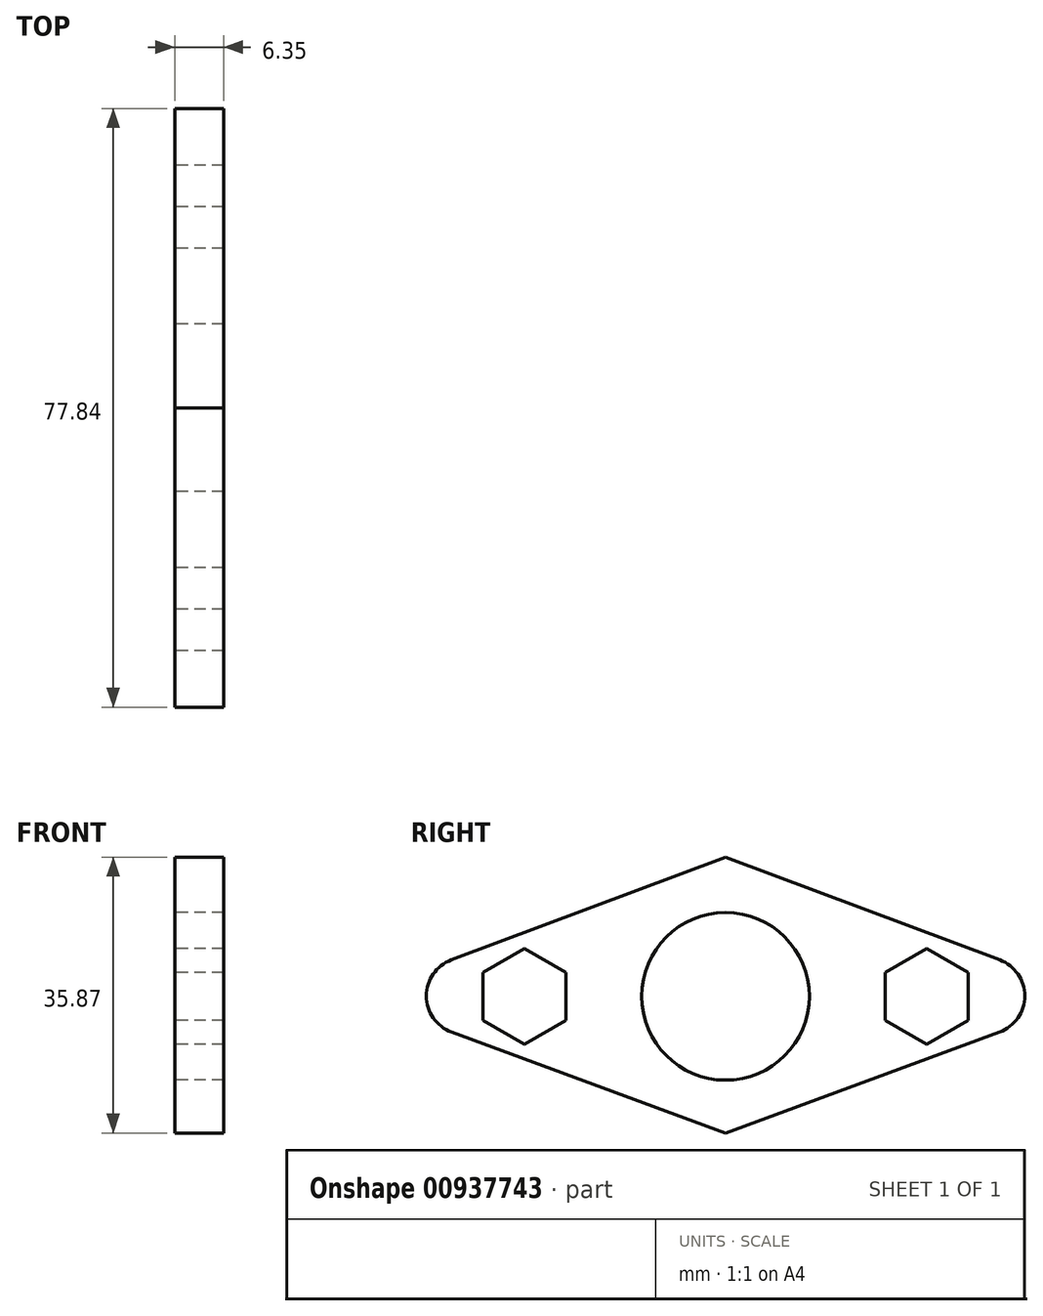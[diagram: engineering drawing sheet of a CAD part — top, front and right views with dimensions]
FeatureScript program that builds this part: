
annotation { "Feature Type Name" : "Feature", "Feature Type Description" : "" }
export const myFeature = defineFeature(function(context is Context, id is Id, definition is map)
    precondition{}
    {
        {
            var Q0;
            Q0=qCreatedBy(makeId("Right.planeOp"),FACE);
            var sketch = newSketch(context, id + "F0", { "sketchPlane" : qUnion([Q0])});
            skPoint(sketch, "E0.start.orphan", {"position": v(-59.2, 0) * mm});
            skPoint(sketch, "E1.end.orphan", {"position": v(60.96, 0) * mm});
            skPoint(sketch, "E2.end.orphan", {"position": v(0, 18.1) * mm});
            skPoint(sketch, "E3.end.orphan", {"position": v(0, -17.77) * mm});
            skCircle(sketch, "E4", {"center": v(0, 0) * mm, "radius": 10.9 * mm});
            skCircle(sketch, "E5.cCircle", {"center": v(26.15, 0) * mm, "radius": 5.4 * mm, "construction": true});
            skLineSegment(sketch, "E5.0", {"start": v(20.75, -3.12) * mm, "end": v(20.75, 3.12) * mm});
            skLineSegment(sketch, "E5.1", {"start": v(20.75, 3.12) * mm, "end": v(26.15, 6.24) * mm});
            skLineSegment(sketch, "E5.2", {"start": v(26.15, 6.24) * mm, "end": v(31.55, 3.12) * mm});
            skLineSegment(sketch, "E5.3", {"start": v(31.55, 3.12) * mm, "end": v(31.55, -3.12) * mm});
            skLineSegment(sketch, "E5.4", {"start": v(31.55, -3.12) * mm, "end": v(26.15, -6.24) * mm});
            skLineSegment(sketch, "E5.5", {"start": v(26.15, -6.24) * mm, "end": v(20.75, -3.12) * mm});
            skCircle(sketch, "E6.MirrorC", {"center": v(-26.15, 0) * mm, "radius": 5.4 * mm, "construction": true});
            skLineSegment(sketch, "E7.MirrorCS", {"start": v(-26.15, -6.24) * mm, "end": v(-20.75, -3.12) * mm});
            skLineSegment(sketch, "E8.MirrorCS", {"start": v(-20.75, -3.12) * mm, "end": v(-20.75, 3.12) * mm});
            skLineSegment(sketch, "E9.MirrorCS", {"start": v(-20.75, 3.12) * mm, "end": v(-26.15, 6.24) * mm});
            skLineSegment(sketch, "E10.MirrorCS", {"start": v(-26.15, 6.24) * mm, "end": v(-31.55, 3.12) * mm});
            skLineSegment(sketch, "E11.MirrorCS", {"start": v(-31.55, 3.12) * mm, "end": v(-31.55, -3.12) * mm});
            skLineSegment(sketch, "E12.MirrorCS", {"start": v(-31.55, -3.12) * mm, "end": v(-26.15, -6.24) * mm});
            skLineSegment(sketch, "E13", {"start": v(0, 18.1) * mm, "end": v(-48.27, 0) * mm});
            skLineSegment(sketch, "E14", {"start": v(-48.27, 0) * mm, "end": v(0, -17.77) * mm});
            skLineSegment(sketch, "E15.MirrorCS", {"start": v(0, 18.1) * mm, "end": v(48.27, 0) * mm});
            skLineSegment(sketch, "E16.MirrorCS", {"start": v(48.27, 0) * mm, "end": v(0, -17.77) * mm});
            skSolve(sketch);
        }
        {
            var Q0;
            Q0=makeQuery(id+"F0.imprint","IMPRINT",FACE,{"disambiguationData":[TD([[makeQuery(id+"F0.imprint","IMPRINT",EDGE,{"derivedFrom":sQuery(id+"F0.wireOp",EDGE,"E4")}),-1.0]])]});
            extrude(context, id + "F1", {"entities" : qUnion([Q0]), "depth" : 6.35 * mm, "offsetDistance" : 25 * mm});
        }
        {
            var Q0;
            Q0=makeQuery(id+"F1.opExtrude","SWEPT_EDGE",EDGE,{"disambiguationData":[OSD([sQuery(id+"F0.wireOp",EDGE,"E13"),sQuery(id+"F0.wireOp",EDGE,"E14")])]});
            var Q1;
            Q1=makeQuery(id+"F1.opExtrude","SWEPT_EDGE",EDGE,{"disambiguationData":[OSD([sQuery(id+"F0.wireOp",EDGE,"E15.MirrorCS"),sQuery(id+"F0.wireOp",EDGE,"E16.MirrorCS")])]});
            fillet(context, id + "F2", {"entities" : qUnion([Q0, Q1]), "radius" : 5 * mm, "tangentPropagation" : true, "allowEdgeOverflow" : false});
        }
    });
